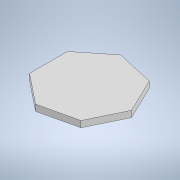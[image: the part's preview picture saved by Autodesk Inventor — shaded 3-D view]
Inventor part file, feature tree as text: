
AUTODESK INVENTOR PART (.ipt)
format: ipt  version: 2022.3 (Build 263350000, 350)  size: 96,256 bytes
history: native  units: in
note: dims shown in document units (in); Inventor stores cm internally (conversion verified against a paired STEP export)
features: extrude x1, sketch x1
ambient origin geometry x8: Origin, YZ Plane, XZ Plane, XY Plane, X Axis, Y Axis, Z Axis, Center Point
bodies: Solid1 (feature_tree)
feature tree (2):
  extrude  "Extrusion1"  Depth=0.1575in TaperAngle=0.0deg
  sketch  "Sketch1"  dims[d0=1.9685in d1=0.1575in d2=0.0in]
